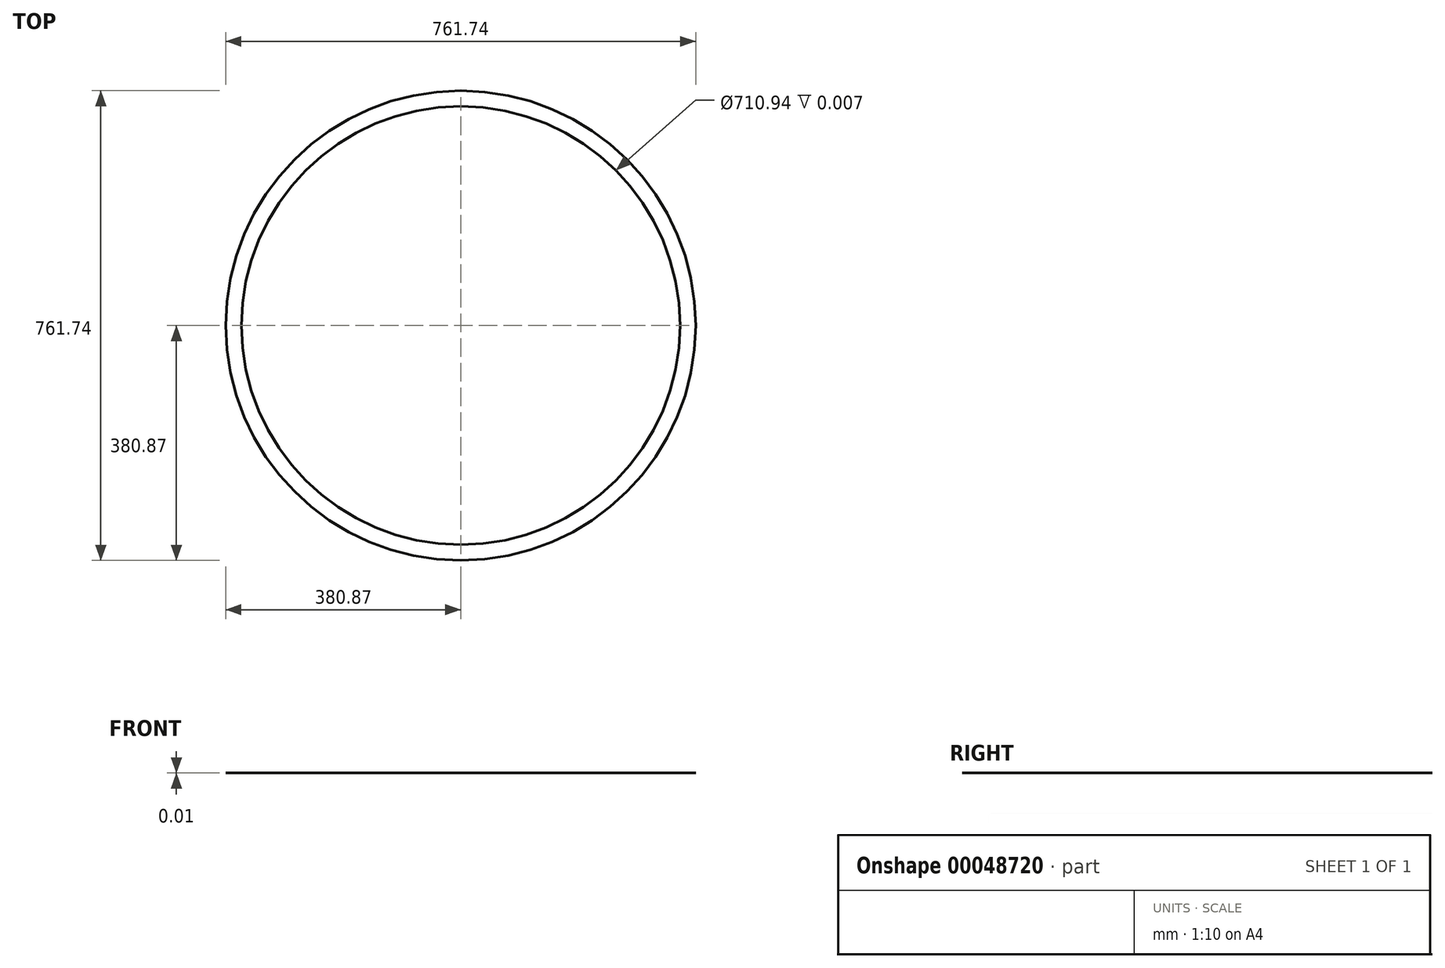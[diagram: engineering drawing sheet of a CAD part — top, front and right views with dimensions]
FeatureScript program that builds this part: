
annotation { "Feature Type Name" : "Feature", "Feature Type Description" : "" }
export const myFeature = defineFeature(function(context is Context, id is Id, definition is map)
    precondition{}
    {
        {
            var Q0;
            Q0=qCreatedBy(makeId("Top.planeOp"),FACE);
            var sketch = newSketch(context, id + "F0", { "sketchPlane" : qUnion([Q0])});
            skCircle(sketch, "E0", {"center": v(0, 0) * mm, "radius": 380.87 * mm});
            skCircle(sketch, "E1", {"center": v(0, 0) * mm, "radius": 355.47 * mm});
            skSolve(sketch);
        }
        {
            var Q0;
            Q0=makeQuery(id+"F0.imprint","IMPRINT",FACE,{"disambiguationData":[TD([[makeQuery(id+"F0.imprint","IMPRINT",EDGE,{"derivedFrom":sQuery(id+"F0.wireOp",EDGE,"E0")}),1.0]])]});
            extrude(context, id + "F1", {"entities" : qUnion([Q0]), "depth" : 3 / 406.4 * mm});
        }
    });
